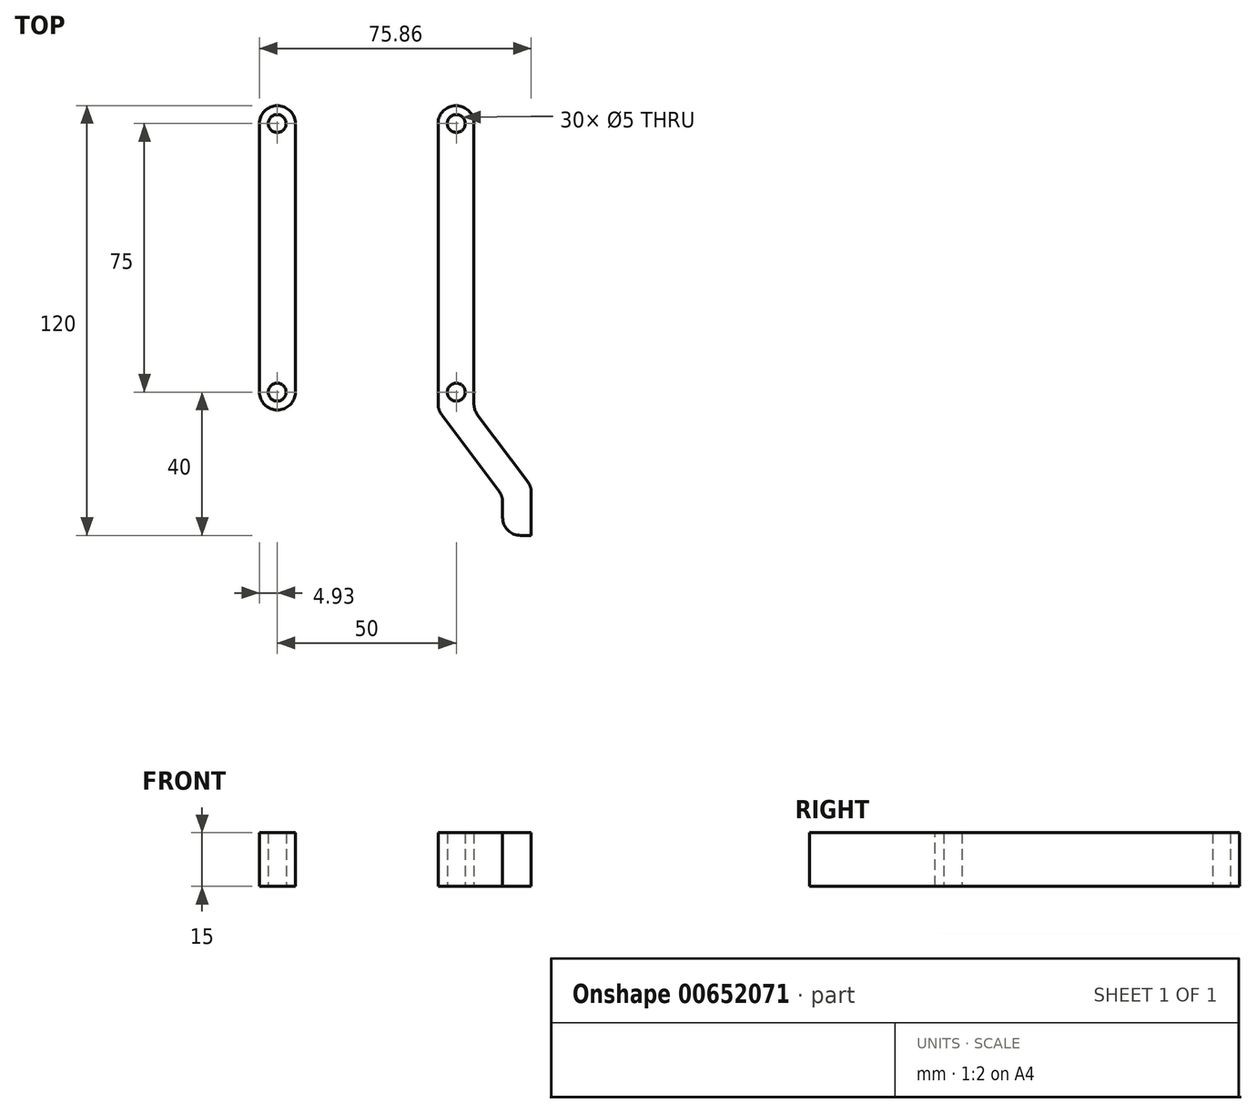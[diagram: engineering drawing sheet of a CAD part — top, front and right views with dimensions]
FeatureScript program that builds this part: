
annotation { "Feature Type Name" : "Feature", "Feature Type Description" : "" }
export const myFeature = defineFeature(function(context is Context, id is Id, definition is map)
    precondition{}
    {
        {
            var Q0;
            Q0=qCreatedBy(makeId("Top.planeOp"),FACE);
            var sketch = newSketch(context, id + "F0", { "sketchPlane" : qUnion([Q0])});
            skCircle(sketch, "E0", {"center": v(0, 0) * mm, "radius": 2.5 * mm});
            skCircle(sketch, "E1", {"center": v(0, 75) * mm, "radius": 2.5 * mm});
            skLineSegment(sketch, "E2.bottom", {"start": v(-4.93, 80) * mm, "end": v(5.07, 80) * mm});
            skLineSegment(sketch, "E2.top", {"start": v(-4.93, -5) * mm, "end": v(5.07, -5) * mm});
            skLineSegment(sketch, "E2.left", {"start": v(-4.93, 80) * mm, "end": v(-4.93, -5) * mm});
            skLineSegment(sketch, "E2.right", {"start": v(5.07, 80) * mm, "end": v(5.07, -5) * mm});
            skSolve(sketch);
        }
        {
            var Q0;
            Q0 = qSketchRegion(id + "F0", true);
            extrude(context, id + "F1", {"entities" : qUnion([Q0]), "depth" : 15 * mm, "offsetDistance" : 25 * mm});
        }
        {
            var Q0;
            Q0=qCreatedBy(makeId("Right.planeOp"),FACE);
            cPlane(context, id + "F2", {"entities" : qUnion([Q0]), "cplaneType" : CPlaneType.OFFSET, "offset" : 25 * mm, "width" : 150 * mm, "height" : 150 * mm});
        }
        {
            var Q0;
            Q0=makeQuery(id+"F1.opExtrude","SWEPT_BODY",BODY,{"disambiguationData":[OSD([sQuery(id+"F0.wireOp",EDGE,"E0"),sQuery(id+"F0.wireOp",EDGE,"E1"),sQuery(id+"F0.wireOp",EDGE,"E2.bottom"),sQuery(id+"F0.wireOp",EDGE,"E2.top"),sQuery(id+"F0.wireOp",EDGE,"E2.left"),sQuery(id+"F0.wireOp",EDGE,"E2.right")])]});
            var Q1;
            Q1=qCreatedBy(id+"F2.planeOp",FACE);
            mirror(context, id + "F3", {"entities" : qUnion([Q0]), "mirrorPlane" : qUnion([Q1])});
        }
        {
            var Q0;
            Q0=qCreatedBy(makeId("Top.planeOp"),FACE);
            var sketch = newSketch(context, id + "F4", { "sketchPlane" : qUnion([Q0])});
            skPoint(sketch, "E3.0", {"position": v(44.93, -5) * mm});
            skPoint(sketch, "E4.0", {"position": v(54.93, -5) * mm});
            skLineSegment(sketch, "E5", {"start": v(44.93, -5) * mm, "end": v(62.93, -29) * mm});
            skLineSegment(sketch, "E6", {"start": v(62.93, -29) * mm, "end": v(62.93, -40) * mm});
            skLineSegment(sketch, "E7", {"start": v(54.93, -5) * mm, "end": v(70.93, -26.33) * mm});
            skLineSegment(sketch, "E8", {"start": v(70.93, -26.33) * mm, "end": v(70.93, -40) * mm});
            skLineSegment(sketch, "E9", {"start": v(62.93, -40) * mm, "end": v(70.93, -40) * mm});
            skLineSegment(sketch, "E10", {"start": v(44.93, -5) * mm, "end": v(54.93, -5) * mm});
            skSolve(sketch);
        }
        {
            var Q0;
            Q0=makeQuery(id+"F4.imprint","IMPRINT",FACE,{"disambiguationData":[TD([[makeQuery(id+"F4.imprint","IMPRINT",EDGE,{"derivedFrom":sQuery(id+"F4.wireOp",EDGE,"E5")}),1.0]])]});
            extrude(context, id + "F5", {"entities" : qUnion([Q0]), "operationType" : NewBodyOperationType.ADD, "depth" : 15 * mm, "offsetDistance" : 25 * mm});
        }
        {
            var Q0;
            Q0=makeQuery(id+"F1.opExtrude","SWEPT_EDGE",EDGE,{"disambiguationData":[OSD([sQuery(id+"F0.wireOp",EDGE,"E2.top"),sQuery(id+"F0.wireOp",EDGE,"E2.right")])]});
            var Q1;
            Q1=makeQuery(id+"F1.opExtrude","SWEPT_EDGE",EDGE,{"disambiguationData":[OSD([sQuery(id+"F0.wireOp",EDGE,"E2.top"),sQuery(id+"F0.wireOp",EDGE,"E2.left")])]});
            var Q2;
            Q2=makeQuery(id+"F5.boolean.opBoolean","MERGE",EDGE,{"derivedFrom":[makeQuery(id+"F3.opPattern","COPY",EDGE,{"derivedFrom":makeQuery(id+"F1.opExtrude","SWEPT_EDGE",EDGE,{"disambiguationData":[OSD([sQuery(id+"F0.wireOp",EDGE,"E2.top"),sQuery(id+"F0.wireOp",EDGE,"E2.right")])]}),"instanceName":"1"}),makeQuery(id+"F5.opExtrude","SWEPT_EDGE",EDGE,{"disambiguationData":[OSD([sQuery(id+"F4.wireOp",EDGE,"E5"),sQuery(id+"F4.wireOp",EDGE,"E10")])]})]});
            var Q3;
            Q3=makeQuery(id+"F5.opExtrude","SWEPT_EDGE",EDGE,{"disambiguationData":[OSD([sQuery(id+"F4.wireOp",EDGE,"E7"),sQuery(id+"F4.wireOp",EDGE,"E8")])]});
            var Q4;
            Q4=makeQuery(id+"F5.opExtrude","SWEPT_EDGE",EDGE,{"disambiguationData":[OSD([sQuery(id+"F4.wireOp",EDGE,"E5"),sQuery(id+"F4.wireOp",EDGE,"E6")])]});
            var Q5;
            Q5=makeQuery(id+"F5.boolean.opBoolean","MERGE",EDGE,{"derivedFrom":[makeQuery(id+"F3.opPattern","COPY",EDGE,{"derivedFrom":makeQuery(id+"F1.opExtrude","SWEPT_EDGE",EDGE,{"disambiguationData":[OSD([sQuery(id+"F0.wireOp",EDGE,"E2.top"),sQuery(id+"F0.wireOp",EDGE,"E2.left")])]}),"instanceName":"1"}),makeQuery(id+"F5.opExtrude","SWEPT_EDGE",EDGE,{"disambiguationData":[OSD([sQuery(id+"F4.wireOp",EDGE,"E7"),sQuery(id+"F4.wireOp",EDGE,"E10")])]})]});
            var Q6;
            Q6=makeQuery(id+"F3.opPattern","COPY",EDGE,{"derivedFrom":makeQuery(id+"F1.opExtrude","SWEPT_EDGE",EDGE,{"disambiguationData":[OSD([sQuery(id+"F0.wireOp",EDGE,"E2.bottom"),sQuery(id+"F0.wireOp",EDGE,"E2.left")])]}),"instanceName":"1"});
            var Q7;
            Q7=makeQuery(id+"F3.opPattern","COPY",EDGE,{"derivedFrom":makeQuery(id+"F1.opExtrude","SWEPT_EDGE",EDGE,{"disambiguationData":[OSD([sQuery(id+"F0.wireOp",EDGE,"E2.bottom"),sQuery(id+"F0.wireOp",EDGE,"E2.right")])]}),"instanceName":"1"});
            var Q8;
            Q8=makeQuery(id+"F1.opExtrude","SWEPT_EDGE",EDGE,{"disambiguationData":[OSD([sQuery(id+"F0.wireOp",EDGE,"E2.bottom"),sQuery(id+"F0.wireOp",EDGE,"E2.right")])]});
            var Q9;
            Q9=makeQuery(id+"F1.opExtrude","SWEPT_EDGE",EDGE,{"disambiguationData":[OSD([sQuery(id+"F0.wireOp",EDGE,"E2.bottom"),sQuery(id+"F0.wireOp",EDGE,"E2.left")])]});
            var Q10;
            Q10=makeQuery(id+"F5.opExtrude","SWEPT_EDGE",EDGE,{"disambiguationData":[OSD([sQuery(id+"F4.wireOp",EDGE,"E6"),sQuery(id+"F4.wireOp",EDGE,"E9")])]});
            fillet(context, id + "F6", {"entities" : qUnion([Q0, Q1, Q2, Q3, Q4, Q5, Q6, Q7, Q8, Q9, Q10]), "radius" : 5 * mm, "tangentPropagation" : true, "allowEdgeOverflow" : false});
        }
    });
